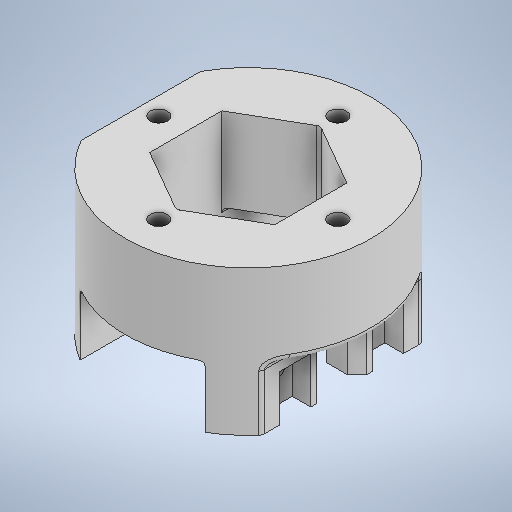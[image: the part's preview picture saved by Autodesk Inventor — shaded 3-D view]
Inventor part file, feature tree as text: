
AUTODESK INVENTOR PART (.ipt)
format: ipt  version: 2025 (Build 290162000, 162)  size: 411,136 bytes
history: native  units: mm
features: sketch x7, extrude x5, hole x2, pattern_circular x2, mirror x2, chamfer x1, fillet x1
ambient origin geometry x8: Origin, YZ Plane, XZ Plane, XY Plane, X Axis, Y Axis, Z Axis, Center Point
bodies: Solid1 (feature_tree)
feature tree (20):
  extrude  "Key Shape"  Depth=36.0mm
  extrude  "Side Walls"  Depth=27.0mm TaperAngle=0.0deg
  hole  "M5 Holes"  [1 undecoded]
  pattern_circular  "Circular Pattern1"  Count=2  [1 undecoded]
  extrude  "M4 Bolt Seats"  Depth=2.0mm
  hole  "M4 Holes"  [1 undecoded]
  mirror  "Mirror1"
  mirror  "Mirror2"
  chamfer  "Chamfer1"  Distance=6.0mm
  extrude  "Nut Seats"  Depth=2.0mm
  pattern_circular  "Circular Pattern2"  [2 undecoded]
  extrude  "Hollow Center"  Depth=10.0mm
  fillet  "Fillet10"  Radius=2.0mm
  sketch  "Sketch1"  dims[d0=82.0mm d1=36.0mm]
  sketch  "Sketch2"  dims[d2=1.25mm d3=27.0mm d4=0.0mm]
  sketch  "Sketch3"  dims[d5=20.25mm d6=10.0mm d7=20.0mm d8=0.0mm]
  sketch  "Sketch4"  dims[d9=5.6mm d10=6.0mm d11=4.0mm d12=2.0mm d13=90.0deg d14=8.0mm d15=20.594885mm d16=29.0mm]
  sketch  "Sketch5"  dims[d17=40.0mm d18=360.0deg d20=10.0mm]
  sketch  "Sketch6"  dims[d21=15.0mm]
  sketch  "Sketch7"  dims[d22=15.0mm d23=6.0mm d24=0.0mm d25=5.25mm d26=6.0mm d27=4.0mm d28=2.0mm d29=90.0deg d30=8.0mm d31=20.594885mm d32=15.0mm d33=10.0mm d40=10.0mm d42=3.0mm d43=2.0mm d44=45.0deg d46=8.15mm d47=4.0mm d48=0.0mm d49=40.0mm d50=360.0deg d52=40.5mm d53=27.0mm d54=0.0mm d55=1.5mm d58=2.0mm]
note: 5 required parameter values undecoded (feature->parameter linkage not recoverable at this tier; creation-order binding heuristic only, values carry confidence <= 0.55)
